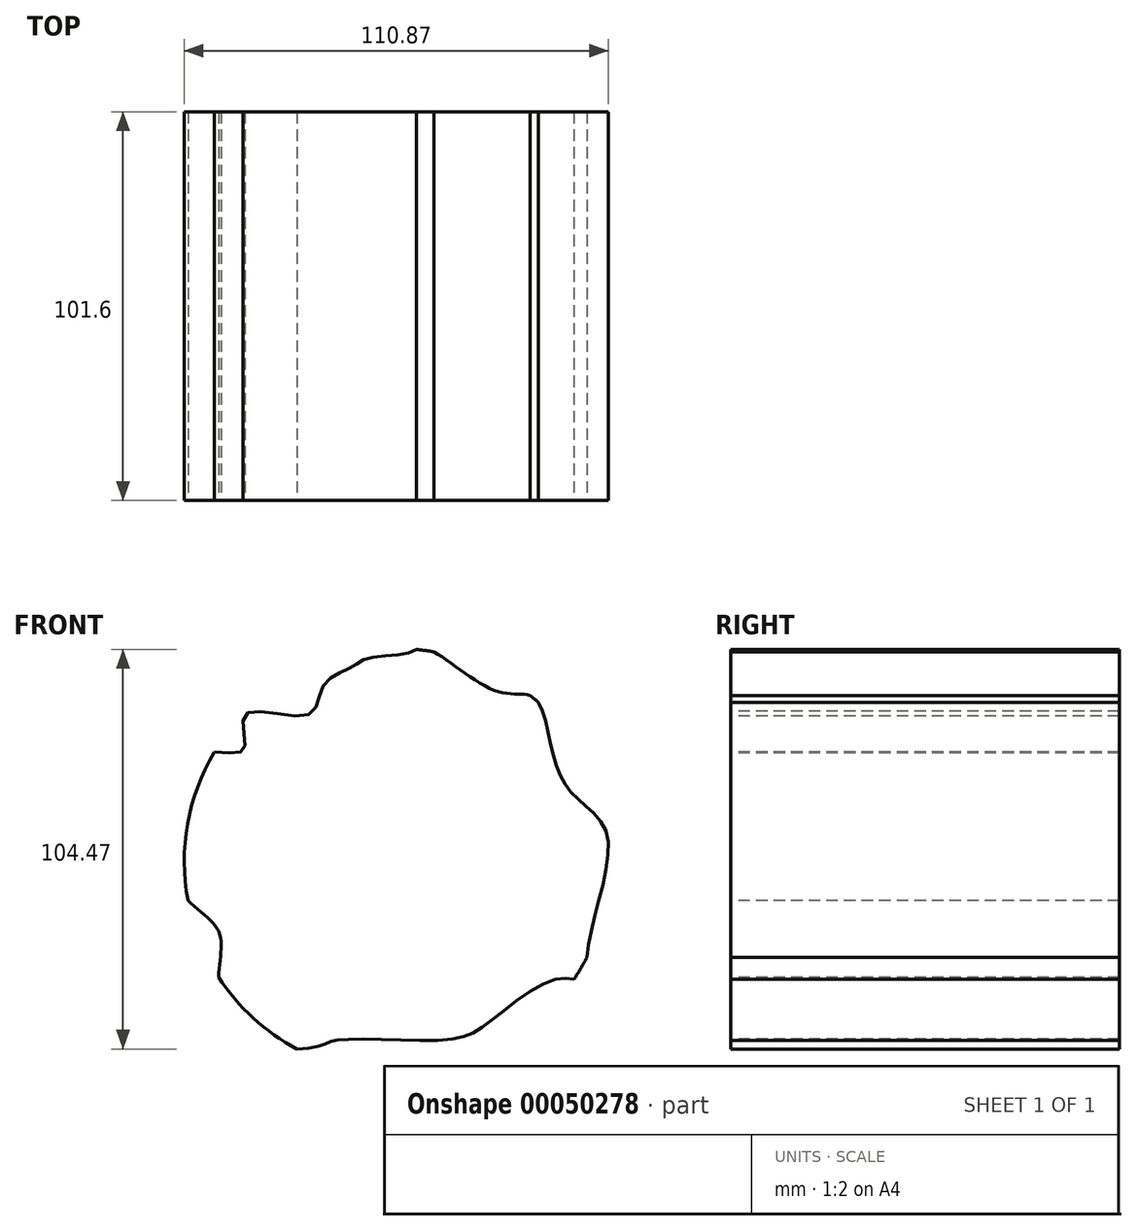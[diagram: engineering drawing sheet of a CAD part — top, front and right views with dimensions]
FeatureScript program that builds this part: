
annotation { "Feature Type Name" : "Feature", "Feature Type Description" : "" }
export const myFeature = defineFeature(function(context is Context, id is Id, definition is map)
    precondition{}
    {
        {
            var Q0;
            Q0=qCreatedBy(makeId("Front.planeOp"),FACE);
            var sketch = newSketch(context, id + "F0", { "sketchPlane" : qUnion([Q0])});
            skCircle(sketch, "E0", {"center": v(0, 0) * mm, "radius": 55.62 * mm});
            skSolve(sketch);
        }
        {
            var Q0;
            Q0=makeQuery(id+"F0.imprint","IMPRINT",FACE,{"disambiguationData":[TD([[makeQuery(id+"F0.imprint","IMPRINT",EDGE,{"derivedFrom":sQuery(id+"F0.wireOp",EDGE,"E0")}),1.0]])]});
            var sketch = newSketch(context, id + "F1", { "sketchPlane" : qUnion([Q0])});
            skFitSpline(sketch, "E1", {"points": [v(-39.66, 38.39) * mm, v(-23.17, 38.39) * mm, v(-19.24, 46.04) * mm, v(-12.37, 50.56) * mm, v(-7.46, 53.11) * mm, v(2.95, 54.49) * mm, v(7.66, 55.66) * mm, v(26.11, 44.47) * mm, v(35.73, 42.9) * mm, v(40.25, 30.34) * mm, v(45.75, 17.77) * mm, v(54.78, 7.36) * mm, v(50.46, -19.73) * mm, v(47.9, -30.73) * mm, v(42.02, -30.73) * mm, v(23.95, -42.12) * mm, v(13.16, -46.63) * mm, v(-14.73, -46.63) * mm, v(-18.85, -47.8) * mm, v(-30.04, -48.6) * mm, v(-46.14, -35.05) * mm, v(-46.53, -18.55) * mm, v(-59.1, -4.22) * mm, v(-53.4, 27.39) * mm, v(-40.05, 29.16) * mm, v(-39.66, 38.39) * mm]});
            skSolve(sketch);
        }
        {
            var Q0;
            {var subQ0=sQuery(id+"F1.wireOp",EDGE,"E1");var subQ1=makeQuery(id+"F0.imprint","IMPRINT",EDGE,{"derivedFrom":sQuery(id+"F0.wireOp",EDGE,"E0")});var subQ9=makeQuery(id+"F1.imprint","INTERSECT",VERTEX,{"disambiguationData":[OD(0.0)],"derivedFrom":[subQ1,subQ0]});Q0=makeQuery(id+"F1.imprint","IMPRINT",FACE,{"disambiguationData":[TD([[makeQuery(id+"F1.imprint","IMPRINT",EDGE,{"disambiguationData":[TD([[subQ9,-1.0]])],"derivedFrom":subQ0}),-1.0]])]});}
            var Q1;
            Q1=sQuery(id+"F1.wireOp",EDGE,"E1");
            extrude(context, id + "F2", {"entities" : qUnion([Q0]), "surfaceEntities" : qUnion([Q1]), "oppositeDirection" : true, "depth" : 101.6 * mm});
        }
    });
